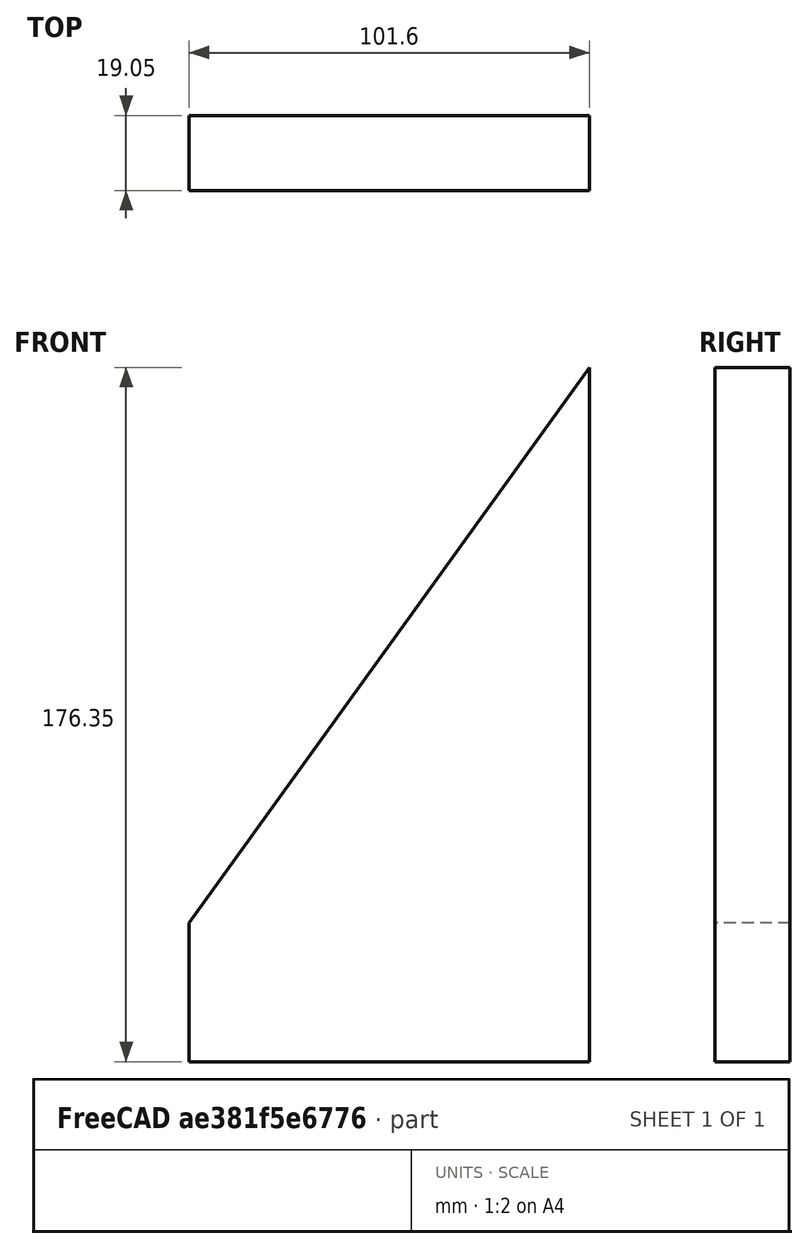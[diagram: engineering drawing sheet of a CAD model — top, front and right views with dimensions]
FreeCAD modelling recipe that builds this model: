
FCSTD DOCUMENT  (FreeCAD 0.19R24291 (Git))
Label: Wedge54.24Degrees
License: All rights reserved
LicenseURL: http://en.wikipedia.org/wiki/All_rights_reserved
objects: TechDraw::DrawViewDimension×4, TechDraw::DrawProjGroupItem×3, Sketcher::SketchObject×1, PartDesign::Pad×1, PartDesign::Body×1, TechDraw::DrawSVGTemplate×1, TechDraw::DrawProjGroup×1, TechDraw::DrawViewAnnotation×1, TechDraw::DrawPage×1
note: 4 computed .brp shape members not serialized (recipe doc carries the construction recipe); baked Part::Feature solids carry a one-line shape summary decoded from their .brp

FEATURE [Sketcher::SketchObject] Sketch
  FullyConstrained = true
  MapMode = 5
  Placement = pos=(0,0,0) rot=(1,0,0;1.5708rad)
  Support = -> [XZ_Plane]
  sketch-geometry (7):
    g0: LineSegment StartX=0 StartY=0 StartZ=0 EndX=127 EndY=0 EndZ=0
    g1: LineSegment StartX=127 StartY=0 StartZ=0 EndX=127 EndY=176.349 EndZ=0
    g2: LineSegment StartX=127 StartY=176.349 StartZ=0 EndX=0 EndY=0 EndZ=0
    g3: LineSegment StartX=127 StartY=176.349 StartZ=0 EndX=127 EndY=0 EndZ=0
    g4: LineSegment StartX=127 StartY=0 StartZ=0 EndX=25.4 EndY=0 EndZ=0
    g5: LineSegment StartX=25.4 StartY=0 StartZ=0 EndX=25.4 EndY=35.2698 EndZ=0
    g6: LineSegment StartX=25.4 StartY=35.2698 StartZ=0 EndX=127 EndY=176.349 EndZ=0
  constraints (18):
    c: Coincident(g-1,g0)
    c: Horizontal(g0)
    c: Coincident(g0,g1)
    c: Vertical(g1)
    c: Coincident(g1,g2)
    c: Coincident(g2,g0)
    c: Angle(g0,g2) = 0.946667
    c: DistanceX(g0,g0) = 127
    c: Coincident(g1,g3)
    c: Coincident(g3,g0)
    c: Coincident(g3,g4)
    c: PointOnObject(g4,g0)
    c: Coincident(g4,g5)
    c: PointOnObject(g5,g2)
    c: Vertical(g5)
    c: Coincident(g5,g6)
    c: Coincident(g6,g3)
    c: DistanceX(g4,g3) = 101.6
FEATURE [PartDesign::Pad] Pad
  Direction = (1,1,1)
  Length = 19.05
  Length2 = 99.9998
  Placement = pos=(0,0,0) rot=(1,0,0;1.5708rad)
  Profile = -> Sketch
  Type = 0
FEATURE [PartDesign::Body] Body  label="BodyWedge54.24Degrees"
  Group = -> [Sketch,Pad]
  Origin = -> Origin
  Tip = -> Pad
FEATURE [TechDraw::DrawSVGTemplate] Template
  Height = 215.9
  Orientation = 1
  Width = 279.4
FEATURE [TechDraw::DrawProjGroupItem] ProjItem  label="Front"
  CoarseView = false
  Direction = (0,-1,0)
  Focus = 100
  HardHidden = false
  IsoCount = 0
  IsoHidden = false
  IsoVisible = false
  LockPosition = true
  Perspective = false
  Rotation = 0
  RotationVector = (1,0,0)
  ScaleType = 2
  SeamHidden = false
  SeamVisible = true
  SmoothHidden = false
  SmoothVisible = true
  Source = -> [Body]
  Type = 0
  X = 0
  XDirection = (1,0,0)
  Y = 0
FEATURE [TechDraw::DrawProjGroupItem] ProjItem001  label="Left"
  CoarseView = false
  Direction = (-1,-1e-16,0)
  Focus = 100
  HardHidden = false
  IsoCount = 0
  IsoHidden = false
  IsoVisible = false
  LockPosition = true
  Perspective = false
  Rotation = 0
  RotationVector = (1,0,0)
  ScaleType = 2
  SeamHidden = false
  SeamVisible = true
  SmoothHidden = false
  SmoothVisible = true
  Source = -> [Body]
  Type = 1
  X = 69.7737
  XDirection = (1e-16,-1,0)
  Y = 0
FEATURE [TechDraw::DrawProjGroupItem] ProjItem002  label="FrontTopLeft"
  CoarseView = false
  Direction = (-0.57735,-0.57735,0.57735)
  Focus = 100
  HardHidden = false
  IsoCount = 0
  IsoHidden = false
  IsoVisible = false
  LockPosition = true
  Perspective = false
  Rotation = 0
  RotationVector = (1,0,0)
  ScaleType = 2
  SeamHidden = false
  SeamVisible = true
  SmoothHidden = false
  SmoothVisible = true
  Source = -> [Body]
  Type = 6
  X = 137.752
  XDirection = (0.707107,-0.707107,0)
  Y = -4.17703
FEATURE [TechDraw::DrawProjGroup] ProjGroup
  Anchor = -> ProjItem
  AutoDistribute = true
  LockPosition = false
  ProjectionType = 0
  Rotation = 0
  ScaleType = 2
  Source = -> [Body]
  Views = -> [ProjItem,ProjItem001,ProjItem002]
  X = 76.0361
  Y = 107.95
  spacingX = 15.0114
  spacingY = 15.0114
FEATURE [TechDraw::DrawViewDimension] Dimension
  Arbitrary = false
  ArbitraryTolerances = false
  EqualTolerance = true
  FormatSpec = %.3f
  FormatSpecOverTolerance = %+.3f
  FormatSpecUnderTolerance = %+.3f
  Inverted = false
  LockPosition = false
  MeasureType = 1
  OverTolerance = 0
  References2D = -> [ProjItem001]
  Rotation = 0
  ScaleType = 2
  TheoreticalExact = false
  Type = 1
  UnderTolerance = 0
  X = 0.748841
  Y = -36.5045
FEATURE [TechDraw::DrawViewDimension] Dimension001
  Arbitrary = false
  ArbitraryTolerances = false
  EqualTolerance = true
  FormatSpec = %.3f
  FormatSpecOverTolerance = %+.3f
  FormatSpecUnderTolerance = %+.3f
  Inverted = false
  LockPosition = false
  MeasureType = 1
  OverTolerance = 0
  References2D = -> [ProjItem001]
  Rotation = 0
  ScaleType = 2
  TheoreticalExact = false
  Type = 2
  UnderTolerance = 0
  X = 9.525
  Y = -70.5397
FEATURE [TechDraw::DrawViewDimension] Dimension002
  Arbitrary = false
  ArbitraryTolerances = false
  EqualTolerance = true
  FormatSpec = %.3f
  FormatSpecOverTolerance = %+.3f
  FormatSpecUnderTolerance = %+.3f
  Inverted = false
  LockPosition = false
  MeasureType = 1
  OverTolerance = 0
  References2D = -> [ProjItem]
  Rotation = 0
  ScaleType = 2
  TheoreticalExact = false
  Type = 1
  UnderTolerance = 0
  X = 3.36979
  Y = -64.2117
FEATURE [TechDraw::DrawViewDimension] Dimension003
  Arbitrary = false
  ArbitraryTolerances = false
  EqualTolerance = true
  FormatSpec = %.3f
  FormatSpecOverTolerance = %+.3f
  FormatSpecUnderTolerance = %+.3f
  Inverted = false
  LockPosition = false
  MeasureType = 1
  OverTolerance = 0
  References2D = -> [ProjItem]
  Rotation = 0
  ScaleType = 2
  TheoreticalExact = false
  Type = 2
  UnderTolerance = 0
  X = 50.8
  Y = 0
FEATURE [TechDraw::DrawViewAnnotation] Annotation
  Font = osifont
  LineSpace = 80
  LockPosition = false
  MaxWidth = -1
  Rotation = 0
  ScaleType = 2
  Text = Wedge 54.24 degrees.
  TextSize = 5.0038
  TextStyle = 0
  X = 61.0716
  Y = 176.095
FEATURE [TechDraw::DrawPage] Page  label="PageWedge54.24Degrees"
  KeepUpdated = true
  NextBalloonIndex = 1
  ProjectionType = 0
  Template = -> Template
  Views = -> [ProjGroup,Dimension,Dimension001,Dimension002,Dimension003,Annotation]
